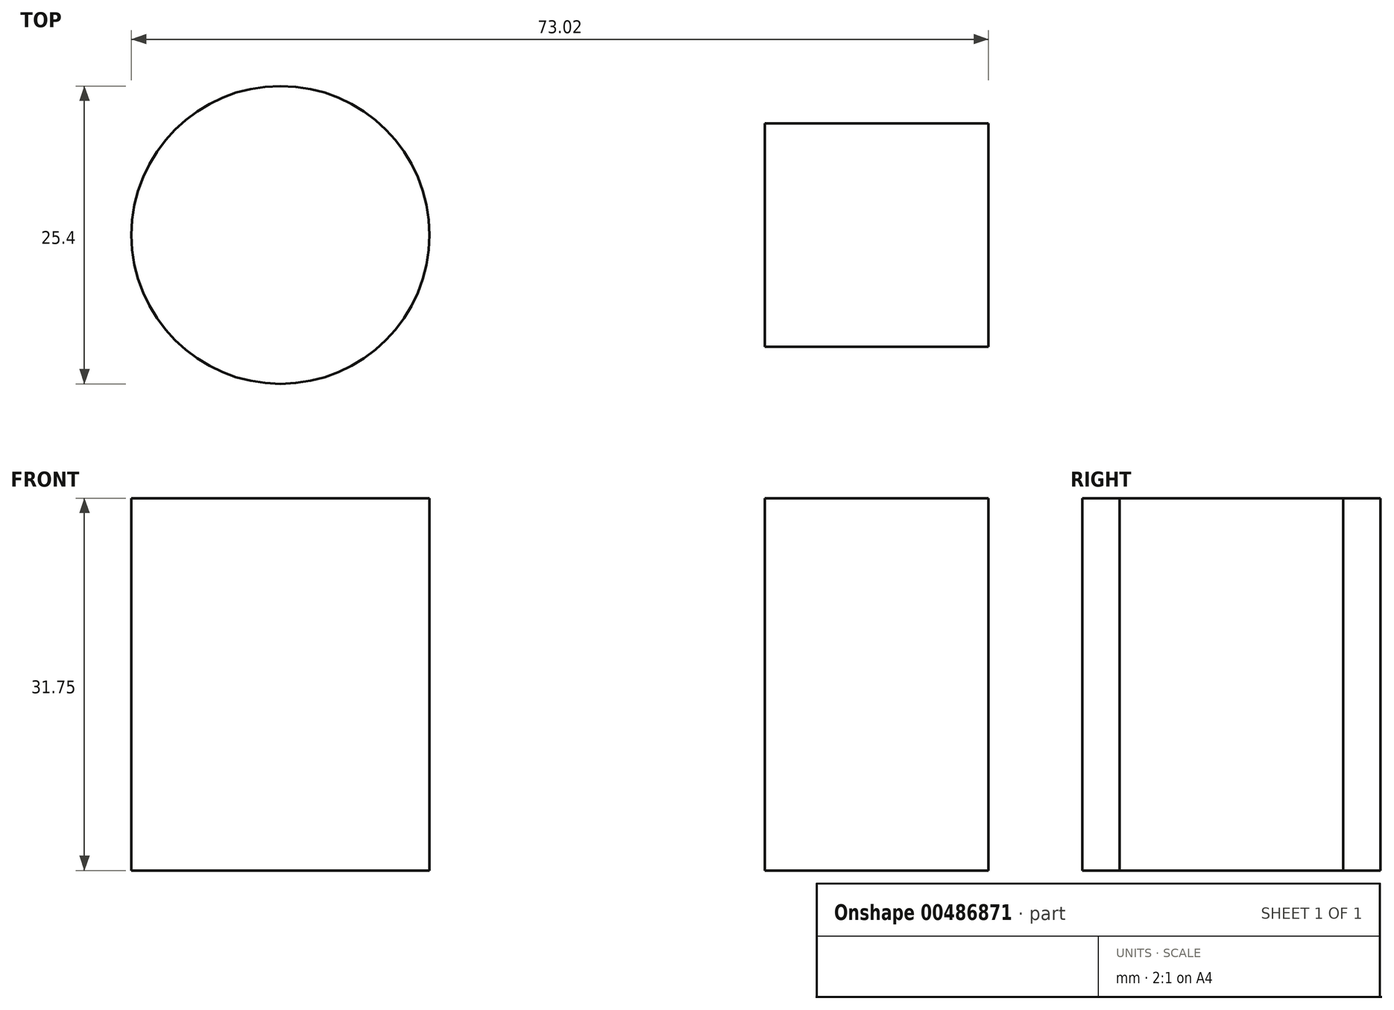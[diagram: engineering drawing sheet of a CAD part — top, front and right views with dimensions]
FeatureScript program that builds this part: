
annotation { "Feature Type Name" : "Feature", "Feature Type Description" : "" }
export const myFeature = defineFeature(function(context is Context, id is Id, definition is map)
    precondition{}
    {
        {
            var Q0;
            Q0=qCreatedBy(makeId("Top.planeOp"),FACE);
            var sketch = newSketch(context, id + "F0", { "sketchPlane" : qUnion([Q0])});
            skLineSegment(sketch, "E0", {"start": v(0, 0) * mm, "end": v(44.45, 0) * mm});
            skLineSegment(sketch, "E1", {"start": v(44.45, 0) * mm, "end": v(44.45, 39.69) * mm});
            skLineSegment(sketch, "E2.bottom", {"start": v(44.45, 39.69) * mm, "end": v(-107.95, 39.69) * mm});
            skLineSegment(sketch, "E2.top", {"start": v(44.45, -39.69) * mm, "end": v(-107.95, -39.69) * mm});
            skLineSegment(sketch, "E2.left", {"start": v(44.45, 39.69) * mm, "end": v(44.45, -39.69) * mm});
            skLineSegment(sketch, "E2.right", {"start": v(-107.95, 39.69) * mm, "end": v(-107.95, -39.69) * mm});
            skLineSegment(sketch, "E3", {"start": v(6.35, 0) * mm, "end": v(-6.35, -22) * mm});
            skLineSegment(sketch, "E4", {"start": v(-6.35, -22) * mm, "end": v(19.05, -22) * mm});
            skLineSegment(sketch, "E5", {"start": v(19.05, -22) * mm, "end": v(6.35, 0) * mm});
            skLineSegment(sketch, "E6.bottom", {"start": v(-41.27, 9.53) * mm, "end": v(-22.22, 9.52) * mm});
            skLineSegment(sketch, "E6.top", {"start": v(-41.27, -9.53) * mm, "end": v(-22.22, -9.53) * mm});
            skLineSegment(sketch, "E6.left", {"start": v(-41.27, 9.53) * mm, "end": v(-41.27, -9.53) * mm});
            skLineSegment(sketch, "E6.right", {"start": v(-22.22, 9.52) * mm, "end": v(-22.22, -9.53) * mm});
            skPoint(sketch, "E6.middle", {"position": v(-31.75, 0) * mm});
            skCircle(sketch, "E7", {"center": v(-82.55, 0) * mm, "radius": 12.7 * mm});
            skSolve(sketch);
        }
        {
            var Q0;
            Q0=makeQuery(id+"F0.imprint","IMPRINT",FACE,{"disambiguationData":[TD([[makeQuery(id+"F0.imprint","IMPRINT",EDGE,{"derivedFrom":sQuery(id+"F0.wireOp",EDGE,"E7")}),1.0]])]});
            var Q1;
            Q1=makeQuery(id+"F0.imprint","IMPRINT",FACE,{"disambiguationData":[TD([[makeQuery(id+"F0.imprint","IMPRINT",EDGE,{"derivedFrom":sQuery(id+"F0.wireOp",EDGE,"E6.bottom")}),-1.0]])]});
            extrude(context, id + "F1", {"entities" : qUnion([Q0, Q1]), "oppositeDirection" : true, "depth" : 31.75 * mm});
        }
    });
